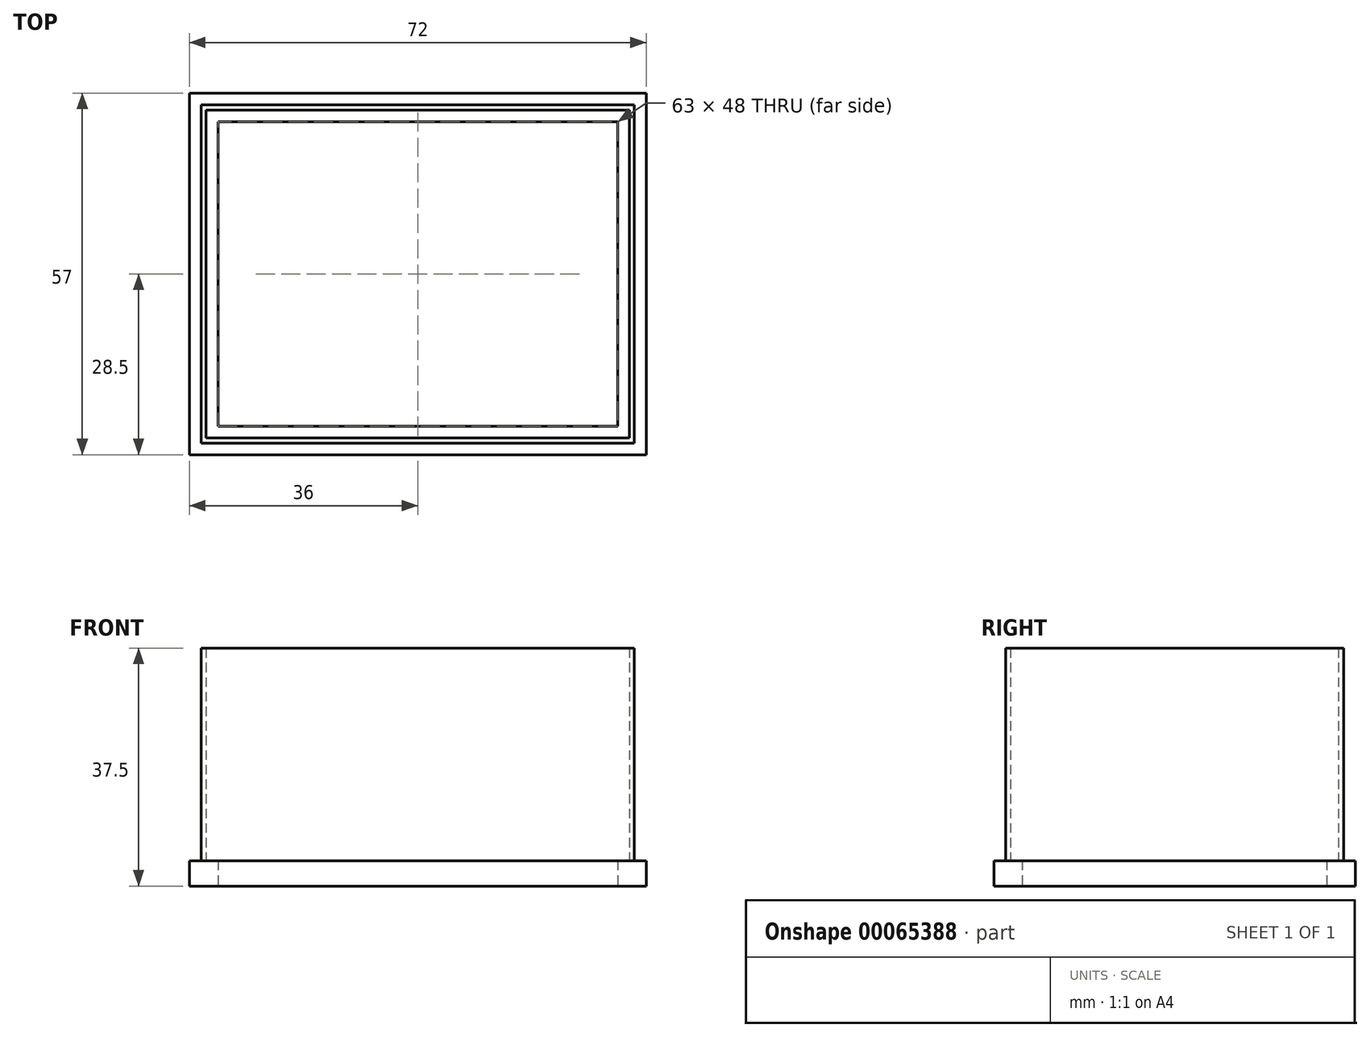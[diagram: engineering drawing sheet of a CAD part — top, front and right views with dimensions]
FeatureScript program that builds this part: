
annotation { "Feature Type Name" : "Feature", "Feature Type Description" : "" }
export const myFeature = defineFeature(function(context is Context, id is Id, definition is map)
    precondition{}
    {
        {
            var Q0;
            Q0=qCreatedBy(makeId("Top.planeOp"),FACE);
            var sketch = newSketch(context, id + "F0", { "sketchPlane" : qUnion([Q0])});
            skLineSegment(sketch, "E0.bottom", {"start": v(36, 28.5) * mm, "end": v(-36, 28.5) * mm});
            skLineSegment(sketch, "E0.top", {"start": v(36, -28.5) * mm, "end": v(-36, -28.5) * mm});
            skLineSegment(sketch, "E0.left", {"start": v(36, 28.5) * mm, "end": v(36, -28.5) * mm});
            skLineSegment(sketch, "E0.right", {"start": v(-36, 28.5) * mm, "end": v(-36, -28.5) * mm});
            skPoint(sketch, "E0.middle", {"position": v(0, 0) * mm});
            skLineSegment(sketch, "E1.bottom", {"start": v(31.5, 24) * mm, "end": v(-31.5, 24) * mm});
            skLineSegment(sketch, "E1.top", {"start": v(31.5, -24) * mm, "end": v(-31.5, -24) * mm});
            skLineSegment(sketch, "E1.left", {"start": v(31.5, 24) * mm, "end": v(31.5, -24) * mm});
            skLineSegment(sketch, "E1.right", {"start": v(-31.5, 24) * mm, "end": v(-31.5, -24) * mm});
            skSolve(sketch);
        }
        {
            var Q0;
            Q0 = qSketchRegion(id + "F0", true);
            extrude(context, id + "F1", {"entities" : qUnion([Q0]), "depth" : 4 * mm});
        }
        {
            var Q0;
            Q0=qCreatedBy(makeId("Top.planeOp"),FACE);
            var sketch = newSketch(context, id + "F2", { "sketchPlane" : qUnion([Q0])});
            skLineSegment(sketch, "E2.bottom", {"start": v(34.15, -26.65) * mm, "end": v(-34.15, -26.65) * mm});
            skLineSegment(sketch, "E2.top", {"start": v(34.15, 26.65) * mm, "end": v(-34.15, 26.65) * mm});
            skLineSegment(sketch, "E2.left", {"start": v(34.15, -26.65) * mm, "end": v(34.15, 26.65) * mm});
            skLineSegment(sketch, "E2.right", {"start": v(-34.15, -26.65) * mm, "end": v(-34.15, 26.65) * mm});
            skPoint(sketch, "E2.middle", {"position": v(0, 0) * mm});
            skLineSegment(sketch, "E3.bottom", {"start": v(-33.35, 25.85) * mm, "end": v(33.35, 25.85) * mm});
            skLineSegment(sketch, "E3.top", {"start": v(-33.35, -25.85) * mm, "end": v(33.35, -25.85) * mm});
            skLineSegment(sketch, "E3.left", {"start": v(-33.35, 25.85) * mm, "end": v(-33.35, -25.85) * mm});
            skLineSegment(sketch, "E3.right", {"start": v(33.35, 25.85) * mm, "end": v(33.35, -25.85) * mm});
            skSolve(sketch);
        }
        {
            var Q0;
            Q0 = qSketchRegion(id + "F2", true);
            extrude(context, id + "F3", {"entities" : qUnion([Q0]), "operationType" : NewBodyOperationType.ADD, "depth" : 37.5 * mm});
        }
    });
